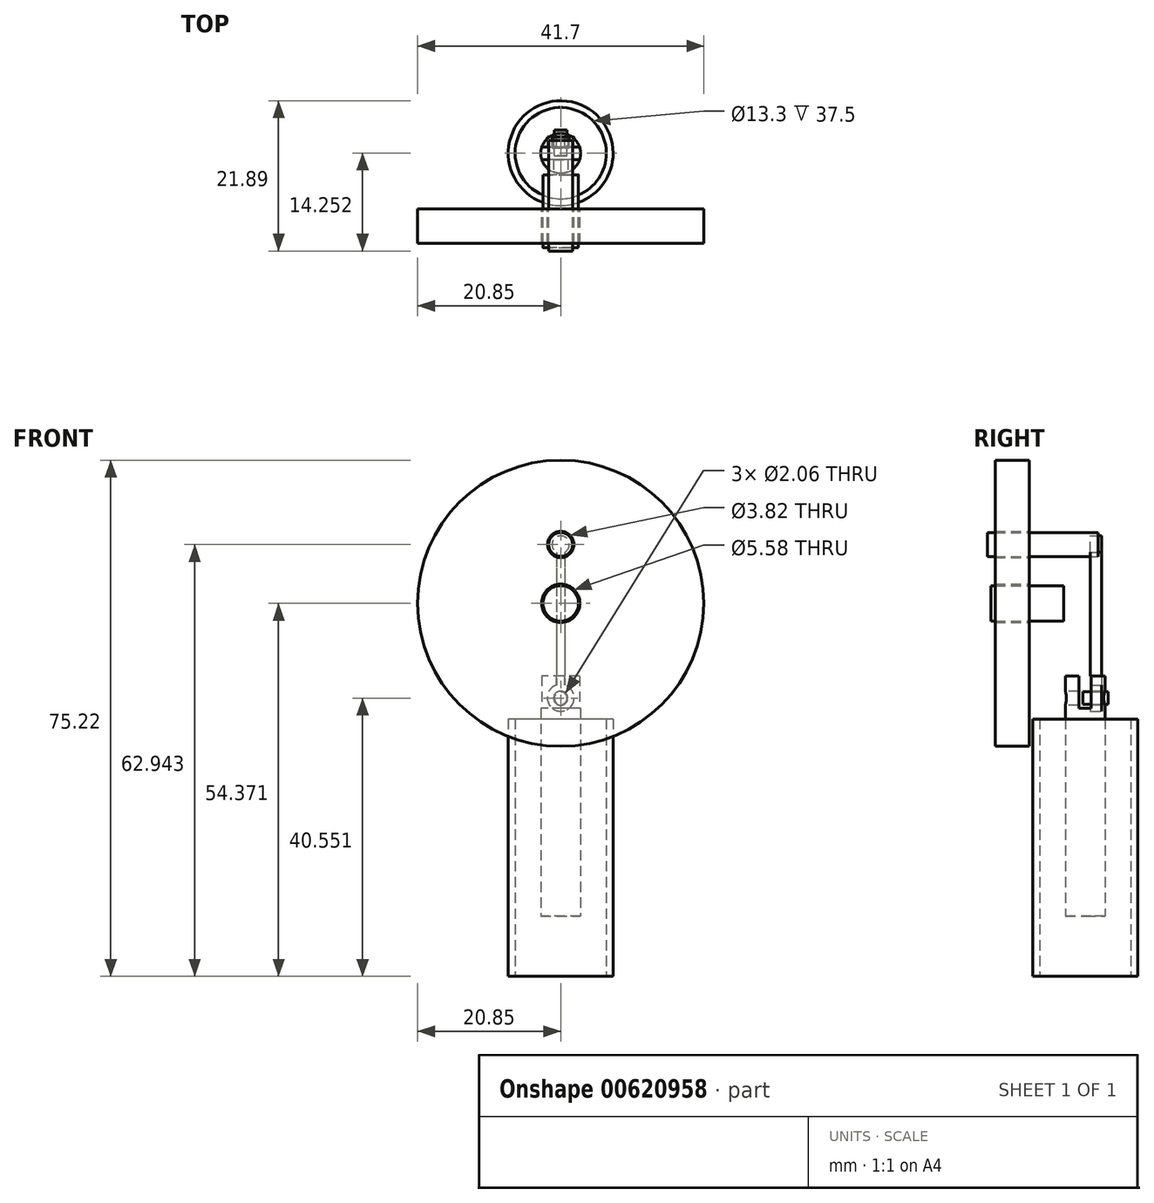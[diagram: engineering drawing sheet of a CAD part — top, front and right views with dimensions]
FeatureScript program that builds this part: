
annotation { "Feature Type Name" : "Feature", "Feature Type Description" : "" }
export const myFeature = defineFeature(function(context is Context, id is Id, definition is map)
    precondition{}
    {
        {
            var Q0;
            Q0=qCreatedBy(makeId("Front.planeOp"),FACE);
            var sketch = newSketch(context, id + "F0", { "sketchPlane" : qUnion([Q0])});
            skCircle(sketch, "E0", {"center": v(0, 35.57) * mm, "radius": 20.85 * mm});
            skCircle(sketch, "E1", {"center": v(0, 44.14) * mm, "radius": 1.91 * mm});
            skCircle(sketch, "E2", {"center": v(0, 35.57) * mm, "radius": 2.8 * mm});
            skSolve(sketch);
        }
        {
            var Q0;
            Q0 = qSketchRegion(id + "F0", true);
            var Q1;
            Q1=makeQuery(id+"F0.imprint","IMPRINT",FACE,{"disambiguationData":[TD([[makeQuery(id+"F0.imprint","IMPRINT",EDGE,{"derivedFrom":sQuery(id+"F0.wireOp",EDGE,"E0")}),1.0]])]});
            extrude(context, id + "F1", {"entities" : qUnion([Q0, Q1]), "depth" : 5 * mm, "offsetDistance" : 25 * mm});
        }
        {
            var Q0;
            Q0=qCreatedBy(makeId("Front.planeOp"),FACE);
            var sketch = newSketch(context, id + "F2", { "sketchPlane" : qUnion([Q0])});
            skCircle(sketch, "E3", {"center": v(0, 35.56) * mm, "radius": 2.6 * mm});
            skSolve(sketch);
        }
        {
            var Q0;
            Q0=makeQuery(id+"F2.imprint","IMPRINT",FACE,{"disambiguationData":[TD([[makeQuery(id+"F2.imprint","IMPRINT",EDGE,{"derivedFrom":sQuery(id+"F2.wireOp",EDGE,"E3")}),1.0]])]});
            extrude(context, id + "F3", {"entities" : qUnion([Q0]), "depth" : 5.6 * mm, "offsetDistance" : 25 * mm, "hasSecondDirection" : true, "secondDirectionOppositeDirection" : true, "secondDirectionDepth" : 5 * mm});
        }
        {
            var Q0;
            Q0=qCreatedBy(makeId("Front.planeOp"),FACE);
            var sketch = newSketch(context, id + "F4", { "sketchPlane" : qUnion([Q0])});
            skCircle(sketch, "E4", {"center": v(0, 44.14) * mm, "radius": 1.74 * mm});
            skSolve(sketch);
        }
        {
            var Q0;
            Q0 = qSketchRegion(id + "F4", true);
            extrude(context, id + "F5", {"entities" : qUnion([Q0]), "depth" : 6.1 * mm, "offsetDistance" : 25 * mm, "hasSecondDirection" : true, "secondDirectionOppositeDirection" : true, "secondDirectionDepth" : 10 * mm});
        }
        {
            var Q0;
            Q0=qCreatedBy(makeId("Top.planeOp"),FACE);
            var sketch = newSketch(context, id + "F6", { "sketchPlane" : qUnion([Q0])});
            skCircle(sketch, "E5", {"center": v(0, 8.15) * mm, "radius": 6.65 * mm});
            skCircle(sketch, "E6", {"center": v(0, 8.15) * mm, "radius": 7.64 * mm});
            skSolve(sketch);
        }
        {
            var Q0;
            Q0 = qSketchRegion(id + "F6", true);
            extrude(context, id + "F7", {"entities" : qUnion([Q0]), "depth" : 18.7 * mm, "offsetDistance" : 25 * mm, "hasSecondDirection" : true, "secondDirectionOppositeDirection" : true, "secondDirectionDepth" : 18.8 * mm});
        }
        {
            var Q0;
            Q0=qCreatedBy(makeId("Top.planeOp"),FACE);
            var sketch = newSketch(context, id + "F8", { "sketchPlane" : qUnion([Q0])});
            skCircle(sketch, "E7", {"center": v(0, 8.13) * mm, "radius": 2.9 * mm});
            skSolve(sketch);
        }
        {
            var Q0;
            Q0=makeQuery(id+"F8.imprint","IMPRINT",FACE,{"disambiguationData":[TD([[makeQuery(id+"F8.imprint","IMPRINT",EDGE,{"derivedFrom":sQuery(id+"F8.wireOp",EDGE,"E7")}),1.0]])]});
            extrude(context, id + "F9", {"entities" : qUnion([Q0]), "depth" : 25 * mm, "offsetDistance" : 25 * mm, "hasSecondDirection" : true, "secondDirectionOppositeDirection" : true, "secondDirectionDepth" : 10 * mm});
        }
        {
            var Q0;
            Q0=qCreatedBy(makeId("Front.planeOp"),FACE);
            cPlane(context, id + "F10", {"entities" : qUnion([Q0]), "cplaneType" : CPlaneType.OFFSET, "offset" : 9.5 * mm, "oppositeDirection" : true, "width" : 150 * mm, "height" : 150 * mm});
        }
        {
            var Q0;
            Q0=qCreatedBy(id+"F10.planeOp",FACE);
            var sketch = newSketch(context, id + "F11", { "sketchPlane" : qUnion([Q0])});
            skLineSegment(sketch, "E8", {"start": v(0, 45.4) * mm, "end": v(0, 44.14) * mm});
            skArc(sketch, "E9", {"start": v(0.6, 43.04) * mm, "mid": v(1.22, 44.46) * mm, "end": v(0, 45.4) * mm});
            skLineSegment(sketch, "E10", {"start": v(0.6, 43.07) * mm, "end": v(0.6, 23.66) * mm});
            skLineSegment(sketch, "E11.MirrorCS", {"start": v(-0.6, 43.07) * mm, "end": v(-0.6, 23.66) * mm});
            skArc(sketch, "E12.MirrorCS", {"start": v(-0.6, 43.04) * mm, "mid": v(-1.22, 44.46) * mm, "end": v(0, 45.4) * mm});
            skArc(sketch, "E13", {"start": v(-0.6, 23.66) * mm, "mid": v(0, 19.85) * mm, "end": v(0.6, 23.66) * mm});
            skPoint(sketch, "E14.MirrorCS.start.orphan", {"position": v(-0.6, 21.8) * mm});
            skPoint(sketch, "E15.start.orphan", {"position": v(0.6, 21.8) * mm});
            skSolve(sketch);
        }
        {
            var Q0;
            Q0 = qSketchRegion(id + "F11", true);
            extrude(context, id + "F12", {"entities" : qUnion([Q0]), "depth" : 0.6 * mm, "offsetDistance" : 25 * mm, "hasSecondDirection" : true, "secondDirectionOppositeDirection" : true, "secondDirectionDepth" : 1 * mm});
        }
        {
            var Q0;
            Q0=makeQuery(id+"F9.opExtrude","CAP_FACE",FACE,{"disambiguationData":[OSD([sQuery(id+"F8.wireOp",EDGE,"E7")])],"isStart":false});
            var sketch = newSketch(context, id + "F13", { "sketchPlane" : qUnion([Q0])});
            skLineSegment(sketch, "E16.bottom", {"start": v(7.23, 7.23) * mm, "end": v(-7.23, 7.23) * mm});
            skLineSegment(sketch, "E16.top", {"start": v(7.23, 9.02) * mm, "end": v(-7.23, 9.02) * mm});
            skLineSegment(sketch, "E16.left", {"start": v(7.23, 7.23) * mm, "end": v(7.23, 9.02) * mm});
            skLineSegment(sketch, "E16.right", {"start": v(-7.23, 7.23) * mm, "end": v(-7.23, 9.02) * mm});
            skPoint(sketch, "E16.middle", {"position": v(0, 8.13) * mm});
            skSolve(sketch);
        }
        {
            var Q0;
            Q0 = qSketchRegion(id + "F13", true);
            extrude(context, id + "F14", {"entities" : qUnion([Q0]), "operationType" : NewBodyOperationType.REMOVE, "oppositeDirection" : true, "depth" : 4.7 * mm, "offsetDistance" : 25 * mm});
        }
        {
            var Q0;
            Q0=qCreatedBy(id+"F10.planeOp",FACE);
            var sketch = newSketch(context, id + "F15", { "sketchPlane" : qUnion([Q0])});
            skCircle(sketch, "E17", {"center": v(0, 21.75) * mm, "radius": 1.03 * mm});
            skSolve(sketch);
        }
        {
            var Q0;
            Q0 = qSketchRegion(id + "F15", true);
            extrude(context, id + "F16", {"entities" : qUnion([Q0]), "operationType" : NewBodyOperationType.REMOVE, "oppositeDirection" : true, "depth" : 7.5 * mm, "offsetDistance" : 25 * mm, "hasSecondDirection" : true, "secondDirectionOppositeDirection" : false, "secondDirectionDepth" : 6.8 * mm});
        }
        {
            var Q0;
            Q0=qCreatedBy(id+"F10.planeOp",FACE);
            var sketch = newSketch(context, id + "F17", { "sketchPlane" : qUnion([Q0])});
            skCircle(sketch, "E18", {"center": v(0, 21.75) * mm, "radius": 0.93 * mm});
            skSolve(sketch);
        }
        {
            var Q0;
            Q0 = qSketchRegion(id + "F17", true);
            extrude(context, id + "F18", {"entities" : qUnion([Q0]), "depth" : 1.7 * mm, "offsetDistance" : 25 * mm, "hasSecondDirection" : true, "secondDirectionOppositeDirection" : true, "secondDirectionDepth" : 2 * mm});
        }
    });
